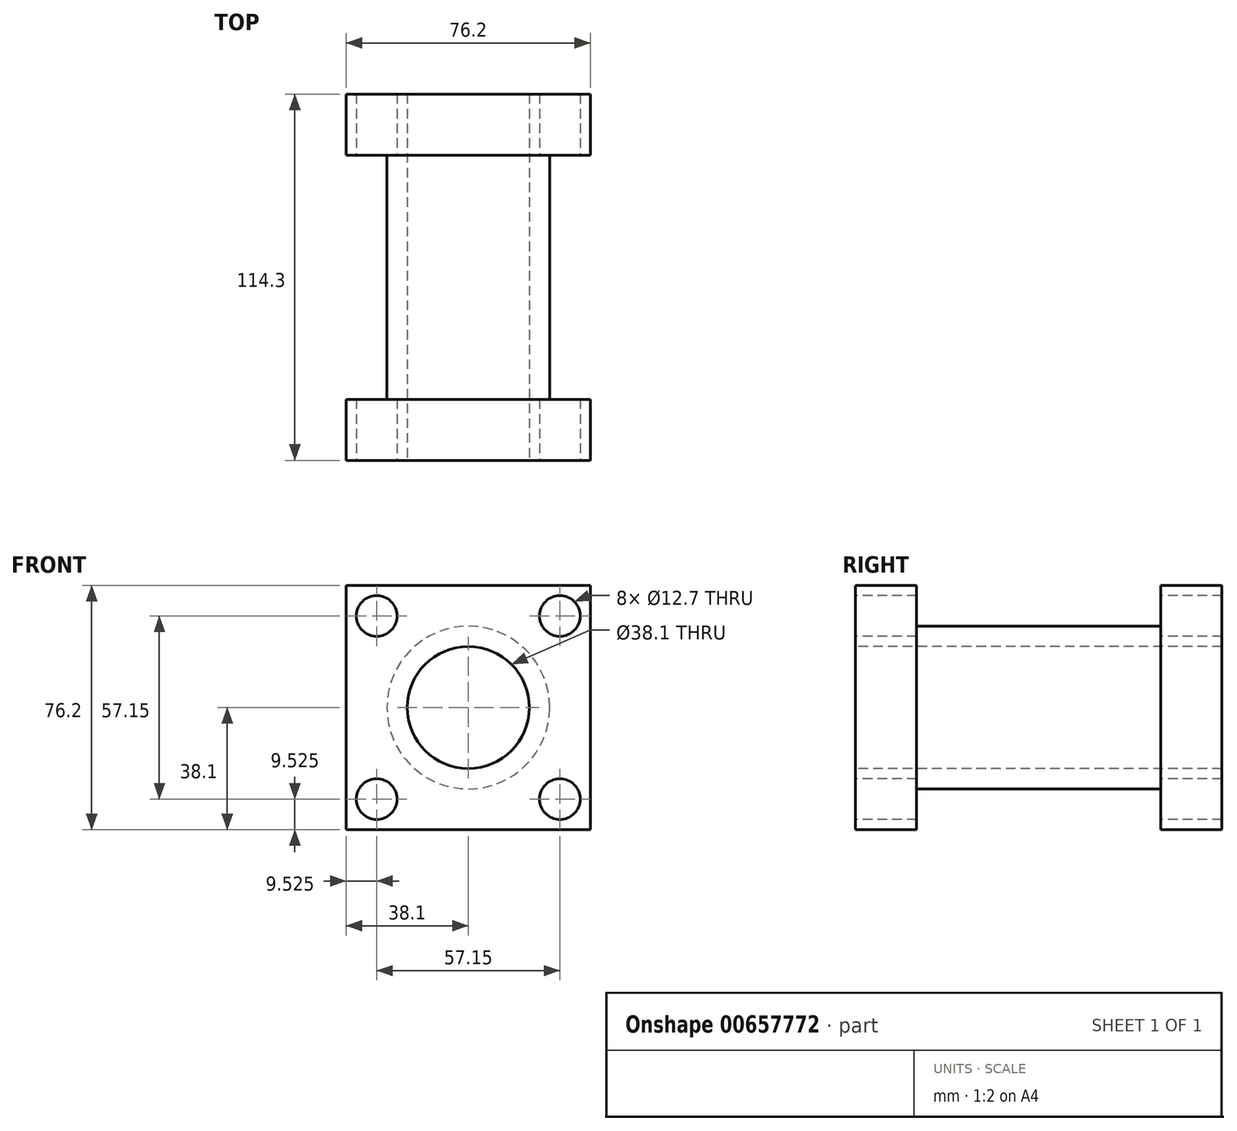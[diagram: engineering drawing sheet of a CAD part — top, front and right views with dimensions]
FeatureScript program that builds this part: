
annotation { "Feature Type Name" : "Feature", "Feature Type Description" : "" }
export const myFeature = defineFeature(function(context is Context, id is Id, definition is map)
    precondition{}
    {
        {
            var Q0;
            Q0=qCreatedBy(makeId("Front.planeOp"),FACE);
            var sketch = newSketch(context, id + "F0", { "sketchPlane" : qUnion([Q0])});
            skLineSegment(sketch, "E0.bottom", {"start": v(38.1, 38.1) * mm, "end": v(-38.1, 38.1) * mm});
            skLineSegment(sketch, "E0.top", {"start": v(38.1, -38.1) * mm, "end": v(-38.1, -38.1) * mm});
            skLineSegment(sketch, "E0.left", {"start": v(38.1, 38.1) * mm, "end": v(38.1, -38.1) * mm});
            skLineSegment(sketch, "E0.right", {"start": v(-38.1, 38.1) * mm, "end": v(-38.1, -38.1) * mm});
            skPoint(sketch, "E0.middle", {"position": v(0, 0) * mm});
            skSolve(sketch);
        }
        {
            var Q0;
            Q0 = qSketchRegion(id + "F0", true);
            extrude(context, id + "F1", {"entities" : qUnion([Q0]), "depth" : 19.05 * mm, "offsetDistance" : 25.4 * mm});
        }
        {
            var Q0;
            Q0=makeQuery(id+"F1.opExtrude","CAP_FACE",FACE,{"disambiguationData":[OSD([sQuery(id+"F0.wireOp",EDGE,"E0.bottom"),sQuery(id+"F0.wireOp",EDGE,"E0.top"),sQuery(id+"F0.wireOp",EDGE,"E0.left"),sQuery(id+"F0.wireOp",EDGE,"E0.right")])],"isStart":true});
            var sketch = newSketch(context, id + "F2", { "sketchPlane" : qUnion([Q0])});
            skCircle(sketch, "E1", {"center": v(0, 0) * mm, "radius": 25.4 * mm});
            skSolve(sketch);
        }
        {
            var Q0;
            Q0 = qSketchRegion(id + "F2", true);
            extrude(context, id + "F3", {"entities" : qUnion([Q0]), "operationType" : NewBodyOperationType.ADD, "depth" : 76.2 * mm, "offsetDistance" : 25.4 * mm});
        }
        {
            var Q0;
            Q0=makeQuery(id+"F3.opExtrude","CAP_FACE",FACE,{"disambiguationData":[OSD([sQuery(id+"F2.wireOp",EDGE,"E1")])],"isStart":false});
            var sketch = newSketch(context, id + "F4", { "sketchPlane" : qUnion([Q0])});
            skLineSegment(sketch, "E2.bottom", {"start": v(38.1, 38.1) * mm, "end": v(-38.1, 38.1) * mm});
            skLineSegment(sketch, "E2.top", {"start": v(38.1, -38.1) * mm, "end": v(-38.1, -38.1) * mm});
            skLineSegment(sketch, "E2.left", {"start": v(38.1, 38.1) * mm, "end": v(38.1, -38.1) * mm});
            skLineSegment(sketch, "E2.right", {"start": v(-38.1, 38.1) * mm, "end": v(-38.1, -38.1) * mm});
            skPoint(sketch, "E2.middle", {"position": v(0, 0) * mm});
            skSolve(sketch);
        }
        {
            var Q0;
            Q0 = qSketchRegion(id + "F4", true);
            extrude(context, id + "F5", {"entities" : qUnion([Q0]), "operationType" : NewBodyOperationType.ADD, "depth" : 19.05 * mm, "offsetDistance" : 25.4 * mm});
        }
        {
            var Q0;
            Q0=makeQuery(id+"F1.opExtrude","CAP_FACE",FACE,{"disambiguationData":[OSD([sQuery(id+"F0.wireOp",EDGE,"E0.bottom"),sQuery(id+"F0.wireOp",EDGE,"E0.top"),sQuery(id+"F0.wireOp",EDGE,"E0.left"),sQuery(id+"F0.wireOp",EDGE,"E0.right")])],"isStart":false});
            var sketch = newSketch(context, id + "F6", { "sketchPlane" : qUnion([Q0])});
            skCircle(sketch, "E3", {"center": v(0, 0) * mm, "radius": 19.05 * mm});
            skSolve(sketch);
        }
        {
            var Q0;
            Q0 = qSketchRegion(id + "F6", true);
            extrude(context, id + "F7", {"entities" : qUnion([Q0]), "operationType" : NewBodyOperationType.REMOVE, "oppositeDirection" : true, "depth" : 122.17 * mm, "offsetDistance" : 25.4 * mm});
        }
        {
            var Q0;
            Q0=makeQuery(id+"F1.opExtrude","CAP_FACE",FACE,{"disambiguationData":[OSD([sQuery(id+"F0.wireOp",EDGE,"E0.bottom"),sQuery(id+"F0.wireOp",EDGE,"E0.top"),sQuery(id+"F0.wireOp",EDGE,"E0.left"),sQuery(id+"F0.wireOp",EDGE,"E0.right")])],"isStart":false});
            var sketch = newSketch(context, id + "F8", { "sketchPlane" : qUnion([Q0])});
            skLineSegment(sketch, "E4", {"start": v(-38.1, 38.1) * mm, "end": v(38.1, -38.1) * mm});
            skCircle(sketch, "E5", {"center": v(-28.58, 28.57) * mm, "radius": 6.35 * mm});
            skSolve(sketch);
        }
        {
            var Q0;
            Q0 = qSketchRegion(id + "F8", true);
            extrude(context, id + "F9", {"entities" : qUnion([Q0]), "operationType" : NewBodyOperationType.REMOVE, "oppositeDirection" : true, "depth" : 125.22 * mm, "offsetDistance" : 25.4 * mm});
        }
        {
            var Q0;
            Q0=makeQuery(id+"F1.opExtrude","CAP_FACE",FACE,{"disambiguationData":[OSD([sQuery(id+"F0.wireOp",EDGE,"E0.bottom"),sQuery(id+"F0.wireOp",EDGE,"E0.top"),sQuery(id+"F0.wireOp",EDGE,"E0.left"),sQuery(id+"F0.wireOp",EDGE,"E0.right")])],"isStart":false});
            var sketch = newSketch(context, id + "F10", { "sketchPlane" : qUnion([Q0])});
            skLineSegment(sketch, "E6", {"start": v(38.1, 38.1) * mm, "end": v(-38.1, -38.1) * mm});
            skCircle(sketch, "E7", {"center": v(28.58, 28.57) * mm, "radius": 6.35 * mm});
            skSolve(sketch);
        }
        {
            var Q0;
            Q0 = qSketchRegion(id + "F10", true);
            extrude(context, id + "F11", {"entities" : qUnion([Q0]), "operationType" : NewBodyOperationType.REMOVE, "oppositeDirection" : true, "depth" : 131.83 * mm, "offsetDistance" : 25.4 * mm});
        }
        {
            var Q0;
            Q0=makeQuery(id+"F1.opExtrude","CAP_FACE",FACE,{"disambiguationData":[OSD([sQuery(id+"F0.wireOp",EDGE,"E0.bottom"),sQuery(id+"F0.wireOp",EDGE,"E0.top"),sQuery(id+"F0.wireOp",EDGE,"E0.left"),sQuery(id+"F0.wireOp",EDGE,"E0.right")])],"isStart":false});
            var sketch = newSketch(context, id + "F12", { "sketchPlane" : qUnion([Q0])});
            skLineSegment(sketch, "E8", {"start": v(-38.1, -38.1) * mm, "end": v(38.1, 38.1) * mm});
            skCircle(sketch, "E9", {"center": v(-28.58, -28.58) * mm, "radius": 6.35 * mm});
            skSolve(sketch);
        }
        {
            var Q0;
            Q0 = qSketchRegion(id + "F12", true);
            extrude(context, id + "F13", {"entities" : qUnion([Q0]), "operationType" : NewBodyOperationType.REMOVE, "oppositeDirection" : true, "depth" : 129.54 * mm, "offsetDistance" : 25.4 * mm});
        }
        {
            var Q0;
            Q0=makeQuery(id+"F1.opExtrude","CAP_FACE",FACE,{"disambiguationData":[OSD([sQuery(id+"F0.wireOp",EDGE,"E0.bottom"),sQuery(id+"F0.wireOp",EDGE,"E0.top"),sQuery(id+"F0.wireOp",EDGE,"E0.left"),sQuery(id+"F0.wireOp",EDGE,"E0.right")])],"isStart":false});
            var sketch = newSketch(context, id + "F14", { "sketchPlane" : qUnion([Q0])});
            skLineSegment(sketch, "E10", {"start": v(-38.1, 38.1) * mm, "end": v(38.1, -38.1) * mm});
            skCircle(sketch, "E11", {"center": v(28.58, -28.58) * mm, "radius": 6.35 * mm});
            skSolve(sketch);
        }
        {
            var Q0;
            Q0 = qSketchRegion(id + "F14", true);
            extrude(context, id + "F15", {"entities" : qUnion([Q0]), "operationType" : NewBodyOperationType.REMOVE, "oppositeDirection" : true, "depth" : 127 * mm, "offsetDistance" : 25.4 * mm});
        }
    });
